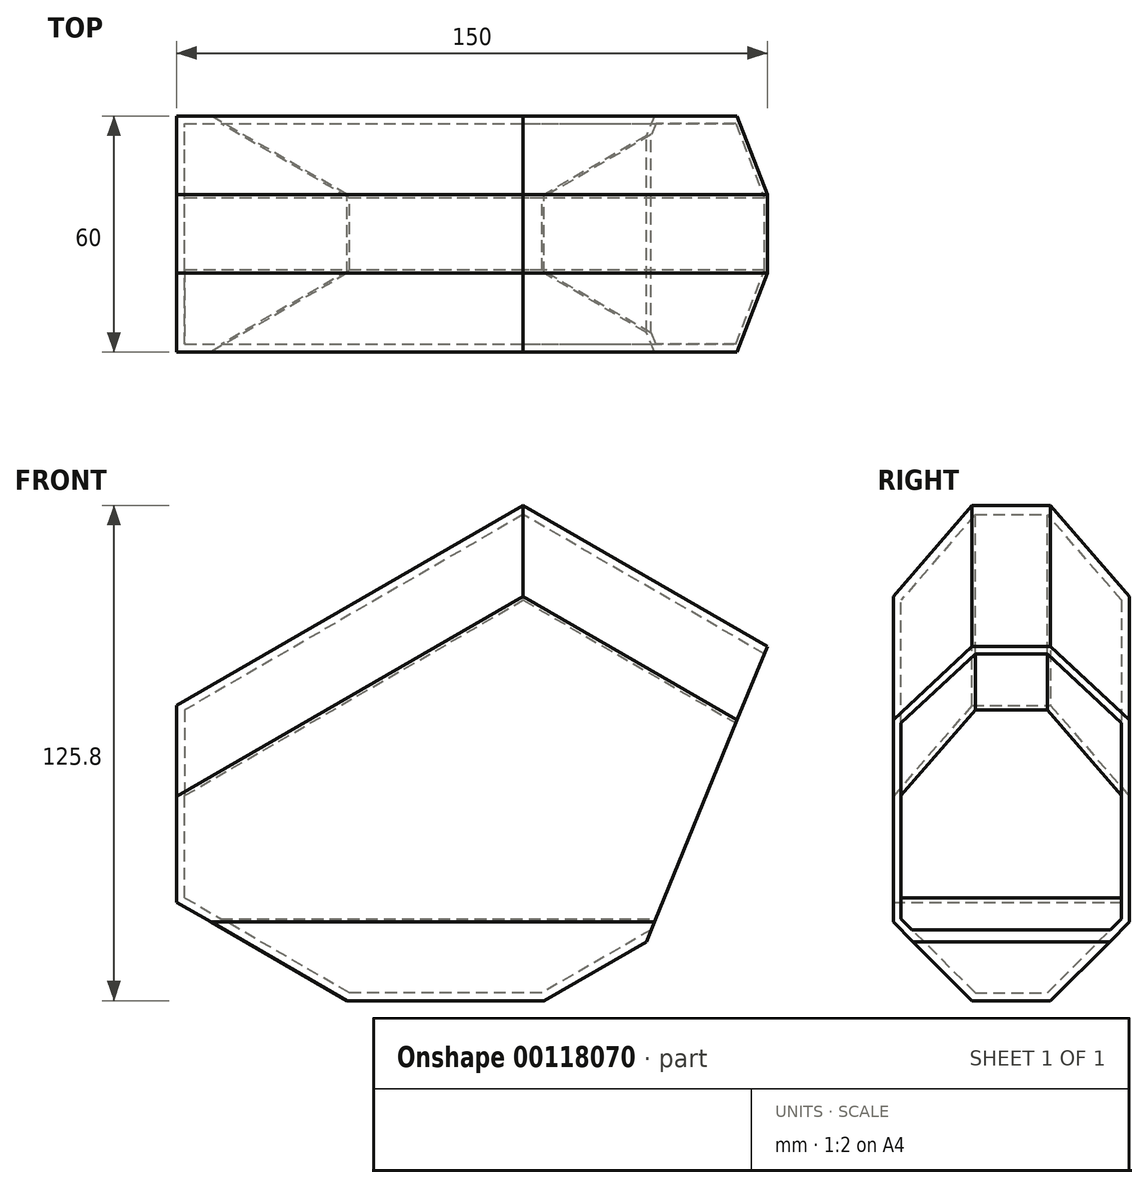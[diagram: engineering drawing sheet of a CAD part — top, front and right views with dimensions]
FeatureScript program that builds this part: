
annotation { "Feature Type Name" : "Feature", "Feature Type Description" : "" }
export const myFeature = defineFeature(function(context is Context, id is Id, definition is map)
    precondition{}
    {
        {
            var Q0;
            Q0=qCreatedBy(makeId("Front.planeOp"),FACE);
            var sketch = newSketch(context, id + "F0", { "sketchPlane" : qUnion([Q0])});
            skLineSegment(sketch, "E0", {"start": v(0, -25) * mm, "end": v(0, 25) * mm});
            skLineSegment(sketch, "E1", {"start": v(0, 25) * mm, "end": v(88, 75.8) * mm});
            skLineSegment(sketch, "E2", {"start": v(88, 75.8) * mm, "end": v(150, 40) * mm});
            skLineSegment(sketch, "E3", {"start": v(0, -25) * mm, "end": v(43.3, -50) * mm});
            skLineSegment(sketch, "E4", {"start": v(43.3, -50) * mm, "end": v(93.3, -50) * mm});
            skLineSegment(sketch, "E5", {"start": v(93.3, -50) * mm, "end": v(119.28, -35) * mm});
            skLineSegment(sketch, "E6", {"start": v(150, 40) * mm, "end": v(119.28, -35) * mm});
            skSolve(sketch);
        }
        {
            var Q0;
            Q0=makeQuery(id+"F0.imprint","IMPRINT",FACE,{"disambiguationData":[TD([[makeQuery(id+"F0.imprint","IMPRINT",EDGE,{"derivedFrom":sQuery(id+"F0.wireOp",EDGE,"E0")}),-1.0]])]});
            extrude(context, id + "F1", {"entities" : qUnion([Q0]), "depth" : 60 * mm, "symmetric" : true});
        }
        {
            var Q0;
            Q0=makeQuery(id+"F1.opExtrude","CAP_EDGE",EDGE,{"disambiguationData":[OSD([sQuery(id+"F0.wireOp",EDGE,"E4")])],"isStart":false});
            var Q1;
            Q1=makeQuery(id+"F1.opExtrude","CAP_EDGE",EDGE,{"disambiguationData":[OSD([sQuery(id+"F0.wireOp",EDGE,"E4")])],"isStart":true});
            var Q2;
            Q2=makeQuery(id+"F1.opExtrude","CAP_EDGE",EDGE,{"disambiguationData":[OSD([sQuery(id+"F0.wireOp",EDGE,"E1")])],"isStart":false});
            var Q3;
            Q3=makeQuery(id+"F1.opExtrude","CAP_EDGE",EDGE,{"disambiguationData":[OSD([sQuery(id+"F0.wireOp",EDGE,"E2")])],"isStart":false});
            var Q4;
            Q4=makeQuery(id+"F1.opExtrude","CAP_EDGE",EDGE,{"disambiguationData":[OSD([sQuery(id+"F0.wireOp",EDGE,"E2")])],"isStart":true});
            var Q5;
            Q5=makeQuery(id+"F1.opExtrude","CAP_EDGE",EDGE,{"disambiguationData":[OSD([sQuery(id+"F0.wireOp",EDGE,"E1")])],"isStart":true});
            chamfer(context, id + "F2", {"entities" : qUnion([Q0, Q1, Q2, Q3, Q4, Q5]), "width" : 20 * mm, "tangentPropagation" : true});
        }
        {
            var Q0;
            Q0=makeQuery(id+"F1.opExtrude","SWEPT_FACE",FACE,{"disambiguationData":[OSD([sQuery(id+"F0.wireOp",EDGE,"E6")])]});
            shell(context, id + "F3", {"entities" : qUnion([Q0]), "thickness" : 2 * mm});
        }
    });
